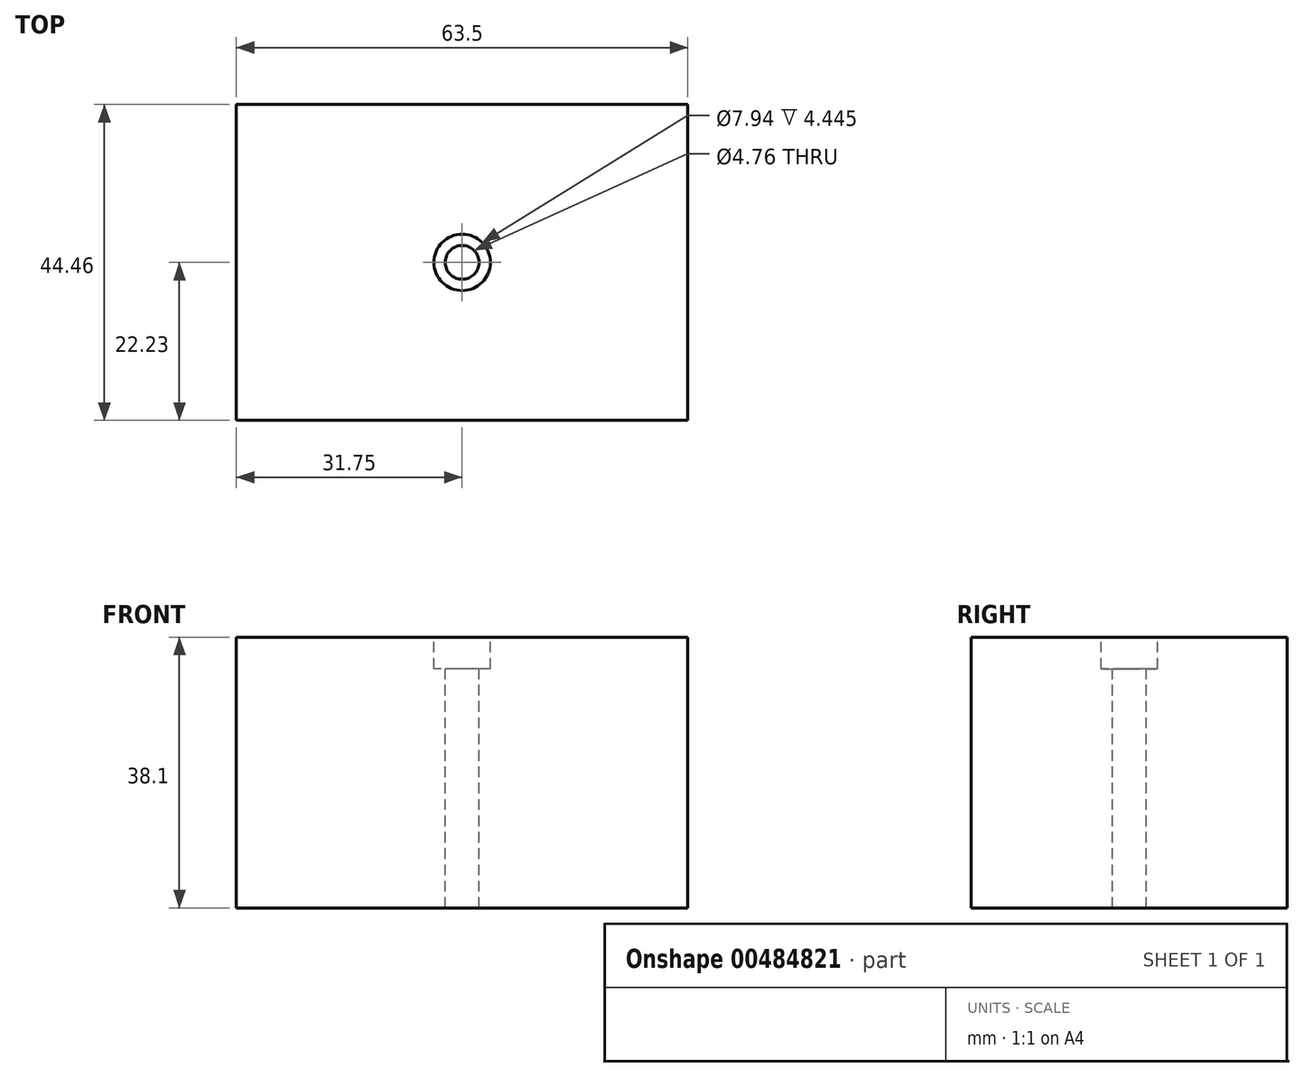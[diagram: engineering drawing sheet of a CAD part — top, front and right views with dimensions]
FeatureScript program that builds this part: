
annotation { "Feature Type Name" : "Feature", "Feature Type Description" : "" }
export const myFeature = defineFeature(function(context is Context, id is Id, definition is map)
    precondition{}
    {
        {
            var Q0;
            Q0=qCreatedBy(makeId("Front.planeOp"),FACE);
            var sketch = newSketch(context, id + "F0", { "sketchPlane" : qUnion([Q0])});
            skLineSegment(sketch, "E0.bottom", {"start": v(-31.75, 19.05) * mm, "end": v(31.75, 19.05) * mm});
            skLineSegment(sketch, "E0.top", {"start": v(-31.75, -19.05) * mm, "end": v(31.75, -19.05) * mm});
            skLineSegment(sketch, "E0.left", {"start": v(-31.75, 19.05) * mm, "end": v(-31.75, -19.05) * mm});
            skLineSegment(sketch, "E0.right", {"start": v(31.75, 19.05) * mm, "end": v(31.75, -19.05) * mm});
            skSolve(sketch);
        }
        {
            var Q0;
            Q0=makeQuery(id+"F0.imprint","IMPRINT",FACE,{"disambiguationData":[TD([[makeQuery(id+"F0.imprint","IMPRINT",EDGE,{"derivedFrom":sQuery(id+"F0.wireOp",EDGE,"E0.bottom")}),-1.0]])]});
            extrude(context, id + "F1", {"entities" : qUnion([Q0]), "depth" : 44.45 * mm, "symmetric" : true});
        }
        {
            var Q0;
            Q0=makeQuery(id+"F1.opExtrude","SWEPT_FACE",FACE,{"disambiguationData":[OSD([sQuery(id+"F0.wireOp",EDGE,"E0.bottom")])]});
            var sketch = newSketch(context, id + "F2", { "sketchPlane" : qUnion([Q0])});
            skCircle(sketch, "E1", {"center": v(0, 0) * mm, "radius": 3.97 * mm});
            skSolve(sketch);
        }
        {
            var Q0;
            Q0=makeQuery(id+"F2.imprint","IMPRINT",FACE,{"disambiguationData":[TD([[makeQuery(id+"F2.imprint","IMPRINT",EDGE,{"derivedFrom":sQuery(id+"F2.wireOp",EDGE,"E1")}),1.0]])]});
            extrude(context, id + "F3", {"entities" : qUnion([Q0]), "operationType" : NewBodyOperationType.REMOVE, "oppositeDirection" : true, "depth" : 4.44 * mm});
        }
        {
            var Q0;
            Q0=makeQuery(id+"F3.boolean.opBoolean","COPY",FACE,{"derivedFrom":makeQuery(id+"F3.opExtrude","CAP_FACE",FACE,{"disambiguationData":[OSD([sQuery(id+"F2.wireOp",EDGE,"E1")])],"isStart":false})});
            var sketch = newSketch(context, id + "F4", { "sketchPlane" : qUnion([Q0])});
            skCircle(sketch, "E2", {"center": v(0, 0) * mm, "radius": 2.38 * mm});
            skSolve(sketch);
        }
        {
            var Q0;
            Q0 = qSketchRegion(id + "F4", true);
            extrude(context, id + "F5", {"entities" : qUnion([Q0]), "operationType" : NewBodyOperationType.REMOVE, "endBound" : BoundingType.THROUGH_ALL, "oppositeDirection" : true, "depth" : 25.4 * mm});
        }
    });
